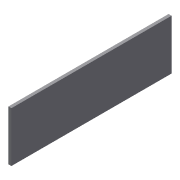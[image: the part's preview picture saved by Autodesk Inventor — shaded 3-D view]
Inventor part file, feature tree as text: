
AUTODESK INVENTOR PART (.ipt)
format: ipt  version: 2014 (Build 180170000, 170)  size: 66,048 bytes
history: native  units: mm
features: extrude x1, sketch x1
ambient origin geometry x8: Origin, YZ Plane, XZ Plane, XY Plane, X Axis, Y Axis, Z Axis, Center Point
bodies: Solid1 (feature_tree)
feature tree (2):
  extrude  "Extrusion1"  Depth=50.0mm
  sketch  "Sketch1"  dims[d0=160.0mm d1=50.0mm d2=3.0mm d3=0.0mm]
